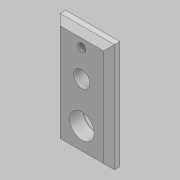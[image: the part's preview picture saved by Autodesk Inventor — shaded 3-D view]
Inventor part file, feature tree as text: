
AUTODESK INVENTOR PART (.ipt)
format: ipt  version: 2018 (Build 220112000, 112)  size: 115,712 bytes
history: native  units: mm
features: extrude x2, chamfer x2, sketch x2, other x1
ambient origin geometry x8: Origin, YZ Plane, XZ Plane, XY Plane, X Axis, Y Axis, Z Axis, Center Point
bodies: Body1 (feature_tree)
feature tree (7):
  other  "實體1"
  extrude  "擠出1"  Depth=30.0mm
  chamfer  "倒角1"  Distance=200.0mm
  extrude  "擠出2"  Depth=100.0mm TaperAngle=0.0deg
  chamfer  "倒角2"  Distance=10.0mm Angle=45.0deg
  sketch  "草圖1"
  sketch  "草圖2"
